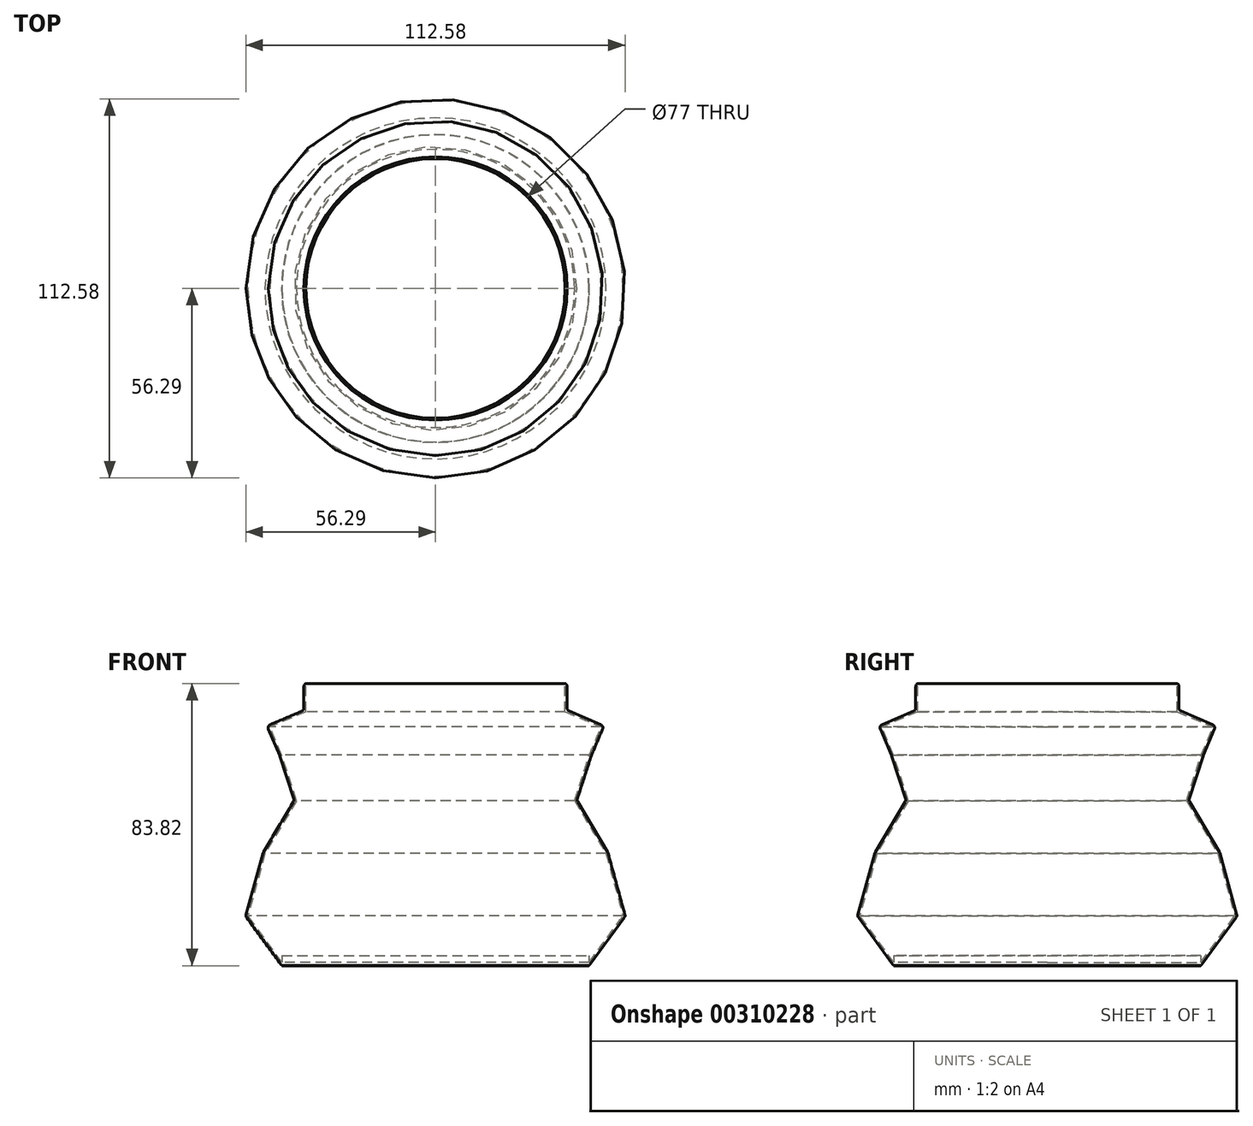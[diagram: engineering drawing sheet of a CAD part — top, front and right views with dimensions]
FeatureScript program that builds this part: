
annotation { "Feature Type Name" : "Feature", "Feature Type Description" : "" }
export const myFeature = defineFeature(function(context is Context, id is Id, definition is map)
    precondition{}
    {
        {
            var Q0;
            Q0=qCreatedBy(makeId("Right.planeOp"),FACE);
            var sketch = newSketch(context, id + "F0", { "sketchPlane" : qUnion([Q0])});
            skLineSegment(sketch, "E0", {"start": v(0, 0) * mm, "end": v(-45.66, 0) * mm});
            skLineSegment(sketch, "E1", {"start": v(-45.66, 0) * mm, "end": v(-56.39, 14.7) * mm});
            skLineSegment(sketch, "E2", {"start": v(-56.39, 14.7) * mm, "end": v(-51.2, 33.56) * mm});
            skLineSegment(sketch, "E3", {"start": v(-51.2, 33.56) * mm, "end": v(-41.96, 49.09) * mm});
            skLineSegment(sketch, "E4", {"start": v(-41.96, 49.09) * mm, "end": v(-46.29, 62.4) * mm});
            skLineSegment(sketch, "E5", {"start": v(-46.29, 62.4) * mm, "end": v(-50.02, 71.2) * mm});
            skLineSegment(sketch, "E6", {"start": v(-50.02, 71.2) * mm, "end": v(-39.1, 75.84) * mm});
            skLineSegment(sketch, "E7", {"start": v(-39.1, 75.84) * mm, "end": v(-39.1, 83.82) * mm});
            skLineSegment(sketch, "E8.0", {"start": v(-38.5, 75.44) * mm, "end": v(-38.5, 83.82) * mm});
            skLineSegment(sketch, "E8.1", {"start": v(-49.24, 70.89) * mm, "end": v(-38.5, 75.44) * mm});
            skLineSegment(sketch, "E8.2", {"start": v(-45.72, 62.61) * mm, "end": v(-49.24, 70.89) * mm});
            skLineSegment(sketch, "E8.3", {"start": v(-41.3, 49.02) * mm, "end": v(-45.72, 62.61) * mm});
            skLineSegment(sketch, "E8.4", {"start": v(0, 0.6) * mm, "end": v(-45.36, 0.6) * mm});
            skLineSegment(sketch, "E8.5", {"start": v(-45.36, 0.6) * mm, "end": v(-55.73, 14.82) * mm});
            skLineSegment(sketch, "E8.6", {"start": v(-55.73, 14.82) * mm, "end": v(-50.65, 33.32) * mm});
            skLineSegment(sketch, "E8.7", {"start": v(-50.65, 33.32) * mm, "end": v(-41.3, 49.02) * mm});
            skLineSegment(sketch, "E9", {"start": v(-39.1, 83.82) * mm, "end": v(-38.5, 83.82) * mm});
            skLineSegment(sketch, "E10", {"start": v(0, 0.6) * mm, "end": v(0, 0) * mm});
            skSolve(sketch);
        }
        {
            var Q0;
            Q0 = qSketchRegion(id + "F0", true);
            var Q1;
            Q1=sQuery(id+"F0.wireOp",EDGE,"E10");
            revolve(context, id + "F1", {"entities" : qUnion([Q0]), "axis" : qUnion([Q1]), "revolveType" : RevolveType.FULL});
        }
        {
            var Q0;
            Q0=makeQuery(id+"F1.opRevolve","SWEPT_EDGE",EDGE,{"disambiguationData":[OSD([sQuery(id+"F0.wireOp",EDGE,"E5"),sQuery(id+"F0.wireOp",EDGE,"E6")])]});
            var Q1;
            Q1=makeQuery(id+"F1.opRevolve","SWEPT_EDGE",EDGE,{"disambiguationData":[OSD([sQuery(id+"F0.wireOp",EDGE,"E2"),sQuery(id+"F0.wireOp",EDGE,"E3")])]});
            var Q2;
            Q2=makeQuery(id+"F1.opRevolve","SWEPT_EDGE",EDGE,{"disambiguationData":[OSD([sQuery(id+"F0.wireOp",EDGE,"E1"),sQuery(id+"F0.wireOp",EDGE,"E2")])]});
            var Q3;
            Q3=makeQuery(id+"F1.opRevolve","SWEPT_EDGE",EDGE,{"disambiguationData":[OSD([sQuery(id+"F0.wireOp",EDGE,"E6"),sQuery(id+"F0.wireOp",EDGE,"E7")])]});
            var Q4;
            Q4=makeQuery(id+"F1.opRevolve","SWEPT_EDGE",EDGE,{"disambiguationData":[OSD([sQuery(id+"F0.wireOp",EDGE,"E3"),sQuery(id+"F0.wireOp",EDGE,"E4")])]});
            var Q5;
            Q5=makeQuery(id+"F1.opRevolve","SWEPT_EDGE",EDGE,{"disambiguationData":[OSD([sQuery(id+"F0.wireOp",EDGE,"E4"),sQuery(id+"F0.wireOp",EDGE,"E5")])]});
            var Q6;
            Q6=makeQuery(id+"F1.opRevolve","SWEPT_EDGE",EDGE,{"disambiguationData":[OSD([sQuery(id+"F0.wireOp",EDGE,"E7"),sQuery(id+"F0.wireOp",EDGE,"E9")])]});
            var Q7;
            Q7=makeQuery(id+"F1.opRevolve","SWEPT_EDGE",EDGE,{"disambiguationData":[OSD([sQuery(id+"F0.wireOp",EDGE,"E0"),sQuery(id+"F0.wireOp",EDGE,"E1")])]});
            fillet(context, id + "F2", {"entities" : qUnion([Q0, Q1, Q2, Q3, Q4, Q5, Q6, Q7]), "radius" : 1 * mm, "tangentPropagation" : true, "allowEdgeOverflow" : false});
        }
        {
            var Q0;
            Q0=makeQuery(id+"F1.opRevolve","SWEPT_FACE",FACE,{"disambiguationData":[OSD([sQuery(id+"F0.wireOp",EDGE,"E0")])]});
            var sketch = newSketch(context, id + "F3", { "sketchPlane" : qUnion([Q0])});
            skCircle(sketch, "E11", {"center": v(0, 0) * mm, "radius": 45.6 * mm});
            skSolve(sketch);
        }
        {
            var Q0;
            Q0 = qSketchRegion(id + "F3", true);
            extrude(context, id + "F4", {"entities" : qUnion([Q0]), "operationType" : NewBodyOperationType.ADD, "oppositeDirection" : true, "depth" : 3 * mm});
        }
    });
